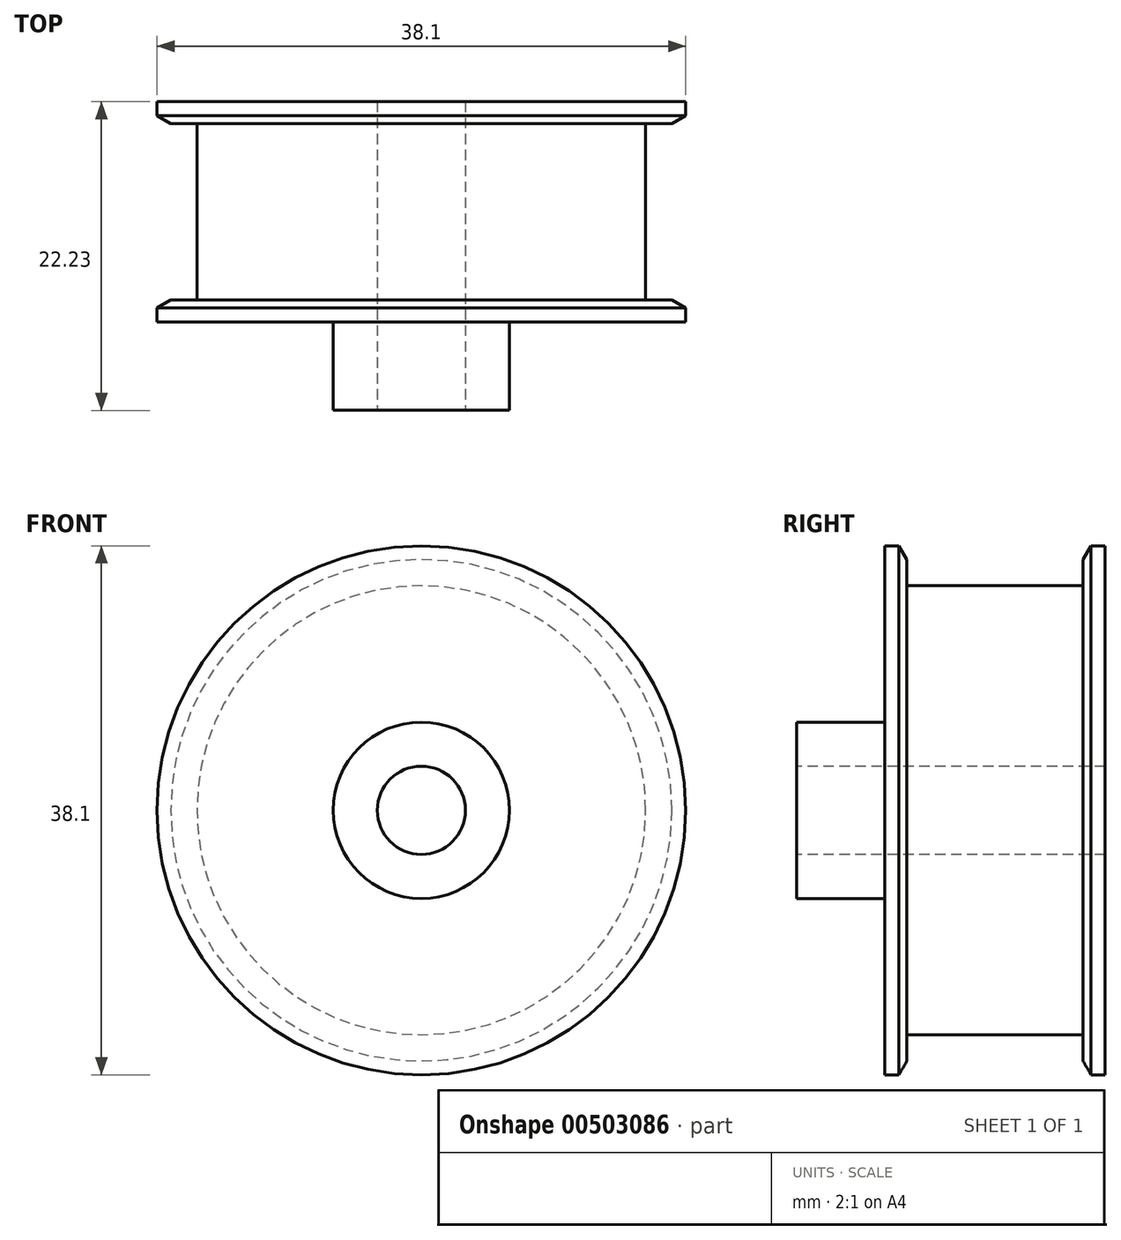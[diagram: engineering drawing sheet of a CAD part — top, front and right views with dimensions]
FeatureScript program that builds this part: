
annotation { "Feature Type Name" : "Feature", "Feature Type Description" : "" }
export const myFeature = defineFeature(function(context is Context, id is Id, definition is map)
    precondition{}
    {
        {
            var Q0;
            Q0=qCreatedBy(makeId("Right.planeOp"),FACE);
            var sketch = newSketch(context, id + "F0", { "sketchPlane" : qUnion([Q0])});
            skLineSegment(sketch, "E0", {"start": v(-14.29, 6.35) * mm, "end": v(-7.94, 6.35) * mm});
            skLineSegment(sketch, "E1", {"start": v(-7.94, 6.35) * mm, "end": v(-7.94, 19.05) * mm});
            skLineSegment(sketch, "E2", {"start": v(-7.94, 19.05) * mm, "end": v(-6.92, 19.05) * mm});
            skLineSegment(sketch, "E3", {"start": v(-6.92, 19.05) * mm, "end": v(-6.35, 18.06) * mm});
            skLineSegment(sketch, "E4", {"start": v(-6.35, 18.06) * mm, "end": v(-6.35, 16.17) * mm});
            skLineSegment(sketch, "E5", {"start": v(-6.35, 16.17) * mm, "end": v(0, 16.17) * mm});
            skLineSegment(sketch, "E6", {"start": v(-14.29, 0) * mm, "end": v(7.94, 0) * mm, "construction": true});
            skLineSegment(sketch, "E7", {"start": v(0, 0) * mm, "end": v(0, 16.17) * mm, "construction": true});
            skLineSegment(sketch, "E8.MirrorCS", {"start": v(6.35, 16.17) * mm, "end": v(0, 16.17) * mm});
            skLineSegment(sketch, "E9.MirrorCS", {"start": v(6.35, 18.06) * mm, "end": v(6.35, 16.17) * mm});
            skLineSegment(sketch, "E10.MirrorCS", {"start": v(6.92, 19.05) * mm, "end": v(6.35, 18.06) * mm});
            skLineSegment(sketch, "E11.MirrorCS", {"start": v(7.94, 19.05) * mm, "end": v(6.92, 19.05) * mm});
            skLineSegment(sketch, "E12.MirrorCS", {"start": v(7.94, 6.35) * mm, "end": v(7.94, 19.05) * mm});
            skLineSegment(sketch, "E13", {"start": v(-14.29, 6.35) * mm, "end": v(-14.29, 3.18) * mm});
            skLineSegment(sketch, "E14", {"start": v(-14.29, 3.18) * mm, "end": v(7.94, 3.18) * mm});
            skLineSegment(sketch, "E15", {"start": v(7.94, 3.18) * mm, "end": v(7.94, 6.35) * mm});
            skSolve(sketch);
        }
        {
            var Q0;
            Q0=makeQuery(id+"F0.imprint","IMPRINT",FACE,{"disambiguationData":[TD([[makeQuery(id+"F0.imprint","IMPRINT",EDGE,{"derivedFrom":sQuery(id+"F0.wireOp",EDGE,"E0")}),-1.0]])]});
            var Q1;
            Q1=sQuery(id+"F0.wireOp",EDGE,"E6");
            revolve(context, id + "F1", {"entities" : qUnion([Q0]), "axis" : qUnion([Q1]), "revolveType" : RevolveType.FULL});
        }
    });
